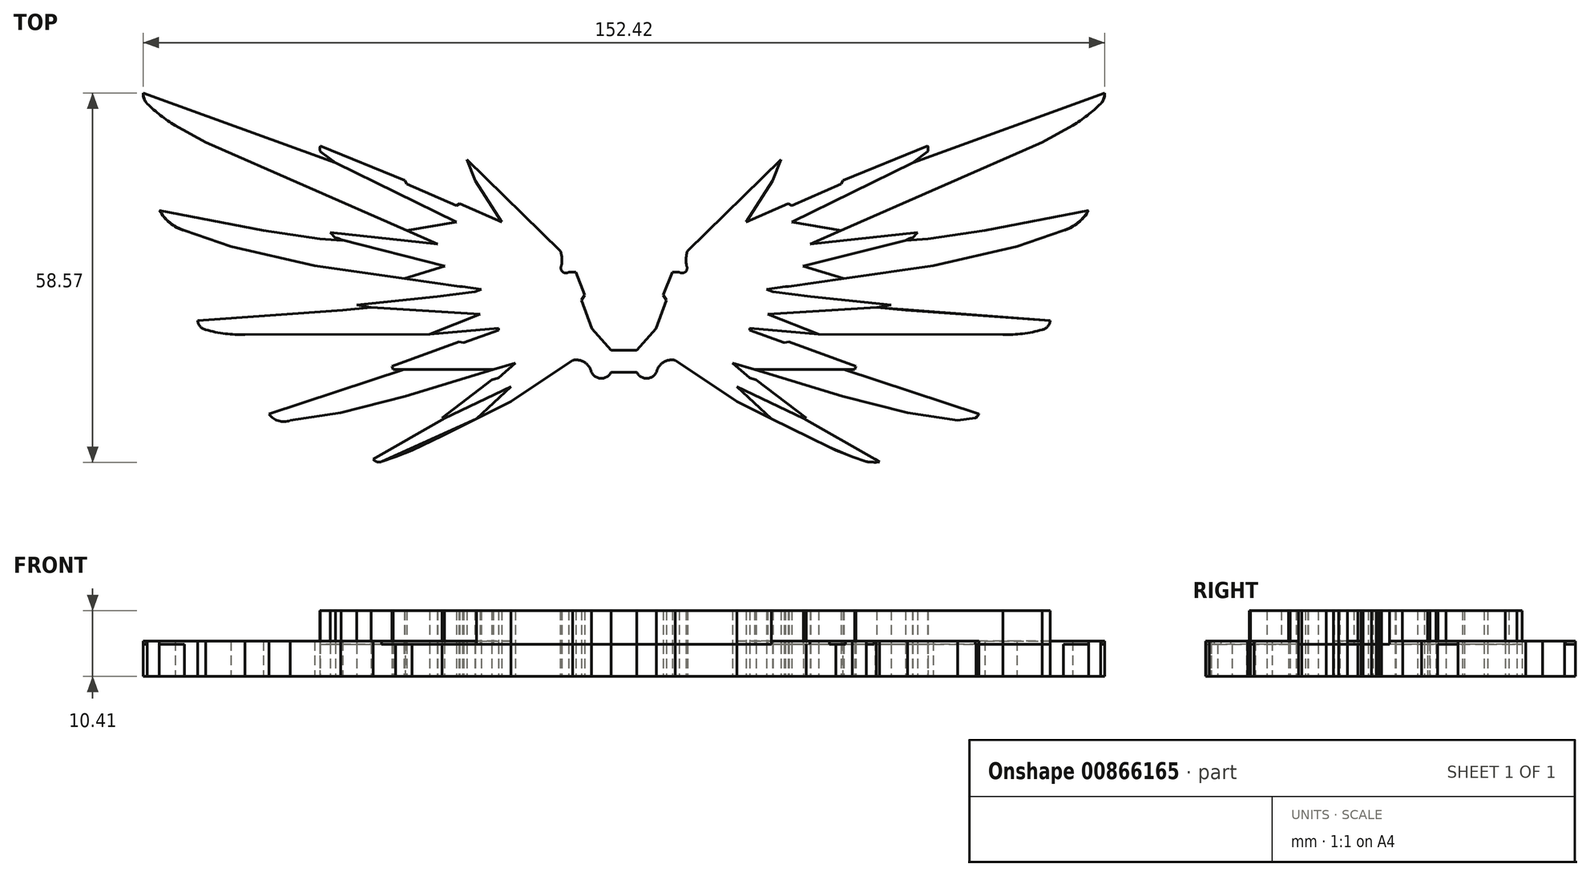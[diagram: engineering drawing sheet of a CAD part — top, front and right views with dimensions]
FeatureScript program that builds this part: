
annotation { "Feature Type Name" : "Feature", "Feature Type Description" : "" }
export const myFeature = defineFeature(function(context is Context, id is Id, definition is map)
    precondition{}
    {
        {
            var Q0;
            Q0=qCreatedBy(makeId("Top.planeOp"),FACE);
            var sketch = newSketch(context, id + "F0", { "sketchPlane" : qUnion([Q0])});
            skLineSegment(sketch, "E0", {"start": v(-45.75, 18.62) * mm, "end": v(-76.2, 29.69) * mm});
            skArc(sketch, "E1", {"start": v(-76.2, 29.69) * mm, "mid": v(-76.09, 28.76) * mm, "end": v(-75.56, 27.98) * mm});
            skArc(sketch, "E2", {"start": v(-75.56, 27.98) * mm, "mid": v(-73.45, 26.13) * mm, "end": v(-71.14, 24.54) * mm});
            skLineSegment(sketch, "E3", {"start": v(-71.14, 24.54) * mm, "end": v(-66.27, 21.85) * mm});
            skLineSegment(sketch, "E4", {"start": v(-66.27, 21.85) * mm, "end": v(-58.56, 18.47) * mm});
            skLineSegment(sketch, "E5", {"start": v(-58.56, 18.47) * mm, "end": v(-35.36, 8.31) * mm});
            skLineSegment(sketch, "E6", {"start": v(-35.36, 8.31) * mm, "end": v(-29.5, 5.75) * mm});
            skLineSegment(sketch, "E7", {"start": v(-29.5, 5.75) * mm, "end": v(-46.28, 7.57) * mm});
            skLineSegment(sketch, "E8", {"start": v(-46.28, 7.57) * mm, "end": v(-46.55, 7.6) * mm});
            skLineSegment(sketch, "E9", {"start": v(-46.55, 7.6) * mm, "end": v(-45.74, 6.68) * mm});
            skArc(sketch, "E10", {"start": v(-44.62, 6.28) * mm, "mid": v(-45.14, 6.59) * mm, "end": v(-45.74, 6.68) * mm});
            skLineSegment(sketch, "E11", {"start": v(-44.62, 6.28) * mm, "end": v(-48.2, 6.59) * mm});
            skLineSegment(sketch, "E12", {"start": v(-48.2, 6.59) * mm, "end": v(-57.18, 7.91) * mm});
            skLineSegment(sketch, "E13", {"start": v(-57.18, 7.91) * mm, "end": v(-73.65, 11.1) * mm});
            skArc(sketch, "E14", {"start": v(-73.65, 11.1) * mm, "mid": v(-71.99, 9.08) * mm, "end": v(-69.68, 7.87) * mm});
            skLineSegment(sketch, "E15", {"start": v(-69.68, 7.87) * mm, "end": v(-62.27, 5.33) * mm});
            skLineSegment(sketch, "E16", {"start": v(-62.27, 5.33) * mm, "end": v(-49, 2.32) * mm});
            skLineSegment(sketch, "E17", {"start": v(-49, 2.32) * mm, "end": v(-26.07, -1) * mm});
            skLineSegment(sketch, "E18", {"start": v(-25.58, -1) * mm, "end": v(-26.07, -1) * mm});
            skLineSegment(sketch, "E19", {"start": v(-25.58, -1) * mm, "end": v(-22.58, -1.44) * mm});
            skLineSegment(sketch, "E20", {"start": v(-22.58, -1.44) * mm, "end": v(-23.6, -1.82) * mm});
            skLineSegment(sketch, "E21", {"start": v(-23.6, -1.82) * mm, "end": v(-29.6, -2.6) * mm});
            skLineSegment(sketch, "E22", {"start": v(-29.6, -2.6) * mm, "end": v(-42.37, -3.94) * mm});
            skLineSegment(sketch, "E23", {"start": v(-42.37, -3.94) * mm, "end": v(-40.05, -4.27) * mm});
            skLineSegment(sketch, "E24", {"start": v(-40.05, -4.27) * mm, "end": v(-44.6, -4.75) * mm});
            skLineSegment(sketch, "E25", {"start": v(-44.6, -4.75) * mm, "end": v(-67.56, -6.41) * mm});
            skArc(sketch, "E26", {"start": v(-67.56, -6.41) * mm, "mid": v(-67.16, -7.34) * mm, "end": v(-66.27, -7.83) * mm});
            skArc(sketch, "E27", {"start": v(-66.27, -7.83) * mm, "mid": v(-63.2, -8.47) * mm, "end": v(-60.07, -8.59) * mm});
            skLineSegment(sketch, "E28", {"start": v(-45.75, 18.62) * mm, "end": v(-48.16, 20.42) * mm});
            skArc(sketch, "E29", {"start": v(-48.16, 21.28) * mm, "mid": v(-48.19, 20.85) * mm, "end": v(-48.16, 20.42) * mm});
            skLineSegment(sketch, "E30", {"start": v(-48.16, 21.28) * mm, "end": v(-34.72, 15.82) * mm});
            skLineSegment(sketch, "E31", {"start": v(-34.72, 15.82) * mm, "end": v(-34.44, 15.24) * mm});
            skLineSegment(sketch, "E32", {"start": v(-34.44, 15.24) * mm, "end": v(-26.57, 11.84) * mm});
            skLineSegment(sketch, "E33", {"start": v(-26.57, 11.84) * mm, "end": v(-26.05, 12.12) * mm});
            skLineSegment(sketch, "E34", {"start": v(-26.05, 12.12) * mm, "end": v(-19.34, 9.23) * mm});
            skLineSegment(sketch, "E35", {"start": v(-19.34, 9.23) * mm, "end": v(-23.55, 15.8) * mm});
            skLineSegment(sketch, "E36", {"start": v(-23.55, 15.8) * mm, "end": v(-24.88, 19.15) * mm});
            skLineSegment(sketch, "E37", {"start": v(-24.88, 19.15) * mm, "end": v(-10.07, 4.67) * mm});
            skArc(sketch, "E38", {"start": v(-9.92, 2.28) * mm, "mid": v(-9.85, 3.48) * mm, "end": v(-10.07, 4.67) * mm});
            skArc(sketch, "E39", {"start": v(-9.92, 2.28) * mm, "mid": v(-9.74, 1.34) * mm, "end": v(-8.79, 1.28) * mm});
            skLineSegment(sketch, "E40", {"start": v(-8.79, 1.28) * mm, "end": v(-7.65, 1.28) * mm});
            skLineSegment(sketch, "E41", {"start": v(-7.65, 1.28) * mm, "end": v(-6.25, -2.35) * mm});
            skLineSegment(sketch, "E42", {"start": v(-6.25, -2.35) * mm, "end": v(-6.74, -3.13) * mm});
            skLineSegment(sketch, "E43", {"start": v(-6.74, -3.13) * mm, "end": v(-5.06, -7.67) * mm});
            skLineSegment(sketch, "E44", {"start": v(-5.06, -7.67) * mm, "end": v(-2.02, -11.07) * mm});
            skLineSegment(sketch, "E45", {"start": v(-2.02, -11.07) * mm, "end": v(-2.02, -12.75) * mm});
            skLineSegment(sketch, "E46", {"start": v(-2.02, -12.75) * mm, "end": v(-2.02, -14.56) * mm});
            skArc(sketch, "E47", {"start": v(-5.16, -14.56) * mm, "mid": v(-3.59, -15.55) * mm, "end": v(-2.02, -14.56) * mm});
            skArc(sketch, "E48", {"start": v(-5.16, -14.56) * mm, "mid": v(-6.25, -13) * mm, "end": v(-8.13, -12.69) * mm});
            skLineSegment(sketch, "E49", {"start": v(-60.07, -8.59) * mm, "end": v(-30.83, -8.52) * mm});
            skLineSegment(sketch, "E50", {"start": v(-30.83, -8.52) * mm, "end": v(-19.9, -7.62) * mm});
            skLineSegment(sketch, "E51", {"start": v(-19.9, -7.62) * mm, "end": v(-19.9, -7.95) * mm});
            skLineSegment(sketch, "E52", {"start": v(-19.9, -7.95) * mm, "end": v(-25.4, -9.9) * mm});
            skLineSegment(sketch, "E53", {"start": v(-25.4, -9.9) * mm, "end": v(-26.18, -9.79) * mm});
            skLineSegment(sketch, "E54", {"start": v(-26.18, -9.79) * mm, "end": v(-36.78, -13.62) * mm});
            skLineSegment(sketch, "E55", {"start": v(-36.78, -13.62) * mm, "end": v(-36.59, -14.16) * mm});
            skLineSegment(sketch, "E56", {"start": v(-36.59, -14.16) * mm, "end": v(-34.87, -14.16) * mm});
            skLineSegment(sketch, "E57", {"start": v(-34.87, -14.16) * mm, "end": v(-56.27, -21.21) * mm});
            skLineSegment(sketch, "E58", {"start": v(-52.88, -22.23) * mm, "end": v(-44.92, -21.03) * mm});
            skLineSegment(sketch, "E59", {"start": v(-44.92, -21.03) * mm, "end": v(-34.68, -18.38) * mm});
            skLineSegment(sketch, "E60", {"start": v(-34.68, -18.38) * mm, "end": v(-17.22, -13.1) * mm});
            skLineSegment(sketch, "E61", {"start": v(-17.22, -13.1) * mm, "end": v(-19.9, -15.47) * mm});
            skLineSegment(sketch, "E62", {"start": v(-19.9, -15.47) * mm, "end": v(-20.95, -15.78) * mm});
            skLineSegment(sketch, "E63", {"start": v(-20.95, -15.78) * mm, "end": v(-28.86, -21.8) * mm});
            skLineSegment(sketch, "E64", {"start": v(-28.86, -21.8) * mm, "end": v(-28.42, -21.87) * mm});
            skLineSegment(sketch, "E65", {"start": v(-28.42, -21.87) * mm, "end": v(-39.78, -28.34) * mm});
            skLineSegment(sketch, "E66", {"start": v(-38.42, -28.77) * mm, "end": v(-36.2, -27.99) * mm});
            skLineSegment(sketch, "E67", {"start": v(-36.2, -27.99) * mm, "end": v(-33.59, -26.98) * mm});
            skLineSegment(sketch, "E68", {"start": v(-33.59, -26.98) * mm, "end": v(-28.86, -24.68) * mm});
            skLineSegment(sketch, "E69", {"start": v(-28.86, -24.68) * mm, "end": v(-17.91, -19.2) * mm});
            skLineSegment(sketch, "E70", {"start": v(-17.91, -19.2) * mm, "end": v(-8.13, -12.69) * mm});
            skLineSegment(sketch, "E71.MirrorCS", {"start": v(46.28, 7.57) * mm, "end": v(46.55, 7.6) * mm});
            skLineSegment(sketch, "E72.MirrorCS", {"start": v(28.86, -21.8) * mm, "end": v(28.42, -21.87) * mm});
            skLineSegment(sketch, "E73.MirrorCS", {"start": v(38.42, -28.77) * mm, "end": v(36.2, -27.99) * mm});
            skLineSegment(sketch, "E74.MirrorCS", {"start": v(34.72, 15.82) * mm, "end": v(34.44, 15.24) * mm});
            skLineSegment(sketch, "E75.MirrorCS", {"start": v(40.03, -28.88) * mm, "end": v(38.42, -28.77) * mm});
            skLineSegment(sketch, "E76.MirrorCS", {"start": v(25.4, -9.9) * mm, "end": v(26.18, -9.79) * mm});
            skArc(sketch, "E77.MirrorCS", {"start": v(44.62, 6.28) * mm, "mid": v(45.14, 6.59) * mm, "end": v(45.74, 6.68) * mm});
            skLineSegment(sketch, "E78.MirrorCS", {"start": v(46.55, 7.6) * mm, "end": v(45.74, 6.68) * mm});
            skLineSegment(sketch, "E79.MirrorCS", {"start": v(40.52, -28.8) * mm, "end": v(40.03, -28.88) * mm});
            skLineSegment(sketch, "E80.MirrorCS", {"start": v(44.62, 6.28) * mm, "end": v(48.2, 6.59) * mm});
            skLineSegment(sketch, "E81.MirrorCS", {"start": v(25.58, -1) * mm, "end": v(26.07, -1) * mm});
            skLineSegment(sketch, "E82.MirrorCS", {"start": v(22.58, -1.44) * mm, "end": v(23.6, -1.82) * mm});
            skLineSegment(sketch, "E83.MirrorCS", {"start": v(39.78, -28.34) * mm, "end": v(40.52, -28.8) * mm});
            skArc(sketch, "E84.MirrorCS", {"start": v(9.92, 2.28) * mm, "mid": v(9.74, 1.34) * mm, "end": v(8.79, 1.28) * mm});
            skLineSegment(sketch, "E85.MirrorCS", {"start": v(25.58, -1) * mm, "end": v(22.58, -1.44) * mm});
            skArc(sketch, "E86.MirrorCS", {"start": v(5.16, -14.56) * mm, "mid": v(3.59, -15.55) * mm, "end": v(2.02, -14.56) * mm});
            skLineSegment(sketch, "E87.MirrorCS", {"start": v(2.02, -12.75) * mm, "end": v(2.02, -14.56) * mm});
            skLineSegment(sketch, "E88.MirrorCS", {"start": v(19.9, -7.62) * mm, "end": v(19.9, -7.95) * mm});
            skLineSegment(sketch, "E89.MirrorCS", {"start": v(8.79, 1.28) * mm, "end": v(7.65, 1.28) * mm});
            skLineSegment(sketch, "E90.MirrorCS", {"start": v(56.27, -21.21) * mm, "end": v(55.84, -21.8) * mm});
            skArc(sketch, "E91.MirrorCS", {"start": v(76.2, 29.69) * mm, "mid": v(76.09, 28.76) * mm, "end": v(75.56, 27.98) * mm});
            skLineSegment(sketch, "E92.MirrorCS", {"start": v(30.83, -8.52) * mm, "end": v(19.9, -7.62) * mm});
            skLineSegment(sketch, "E93.MirrorCS", {"start": v(36.2, -27.99) * mm, "end": v(33.59, -26.98) * mm});
            skLineSegment(sketch, "E94.MirrorCS", {"start": v(23.6, -1.82) * mm, "end": v(29.6, -2.6) * mm});
            skLineSegment(sketch, "E95.MirrorCS", {"start": v(40.05, -4.27) * mm, "end": v(44.6, -4.75) * mm});
            skLineSegment(sketch, "E96.MirrorCS", {"start": v(42.37, -3.94) * mm, "end": v(40.05, -4.27) * mm});
            skLineSegment(sketch, "E97.MirrorCS", {"start": v(5.06, -7.67) * mm, "end": v(2.02, -11.07) * mm});
            skLineSegment(sketch, "E98.MirrorCS", {"start": v(55.84, -21.8) * mm, "end": v(52.88, -22.23) * mm});
            skLineSegment(sketch, "E99.MirrorCS", {"start": v(36.78, -13.62) * mm, "end": v(36.59, -14.16) * mm});
            skLineSegment(sketch, "E100.MirrorCS", {"start": v(19.9, -15.47) * mm, "end": v(20.95, -15.78) * mm});
            skArc(sketch, "E101.MirrorCS", {"start": v(73.65, 11.1) * mm, "mid": v(71.99, 9.08) * mm, "end": v(69.68, 7.87) * mm});
            skLineSegment(sketch, "E102.MirrorCS", {"start": v(35.36, 8.31) * mm, "end": v(29.5, 5.75) * mm});
            skLineSegment(sketch, "E103.MirrorCS", {"start": v(45.75, 18.62) * mm, "end": v(48.16, 20.42) * mm});
            skArc(sketch, "E104.MirrorCS", {"start": v(66.27, -7.83) * mm, "mid": v(63.2, -8.47) * mm, "end": v(60.07, -8.59) * mm});
            skLineSegment(sketch, "E105.MirrorCS", {"start": v(19.34, 9.23) * mm, "end": v(23.55, 15.8) * mm});
            skLineSegment(sketch, "E106.MirrorCS", {"start": v(6.74, -3.13) * mm, "end": v(5.06, -7.67) * mm});
            skLineSegment(sketch, "E107.MirrorCS", {"start": v(33.59, -26.98) * mm, "end": v(28.86, -24.68) * mm});
            skLineSegment(sketch, "E108.MirrorCS", {"start": v(56.27, -21.21) * mm, "end": v(56.27, -21.21) * mm});
            skLineSegment(sketch, "E109.MirrorCS", {"start": v(71.14, 24.54) * mm, "end": v(66.27, 21.85) * mm});
            skLineSegment(sketch, "E110.MirrorCS", {"start": v(6.25, -2.35) * mm, "end": v(6.74, -3.13) * mm});
            skLineSegment(sketch, "E111.MirrorCS", {"start": v(19.9, -7.95) * mm, "end": v(25.4, -9.9) * mm});
            skArc(sketch, "E112.MirrorCS", {"start": v(75.56, 27.98) * mm, "mid": v(73.45, 26.13) * mm, "end": v(71.14, 24.54) * mm});
            skArc(sketch, "E113.MirrorCS", {"start": v(48.16, 21.28) * mm, "mid": v(48.19, 20.85) * mm, "end": v(48.16, 20.42) * mm});
            skArc(sketch, "E114.MirrorCS", {"start": v(5.16, -14.56) * mm, "mid": v(6.25, -13) * mm, "end": v(8.13, -12.69) * mm});
            skLineSegment(sketch, "E115.MirrorCS", {"start": v(36.59, -14.16) * mm, "end": v(34.87, -14.16) * mm});
            skArc(sketch, "E116.MirrorCS", {"start": v(67.56, -6.41) * mm, "mid": v(67.16, -7.34) * mm, "end": v(66.27, -7.83) * mm});
            skLineSegment(sketch, "E117.MirrorCS", {"start": v(17.22, -13.1) * mm, "end": v(19.9, -15.47) * mm});
            skLineSegment(sketch, "E118.MirrorCS", {"start": v(26.57, 11.84) * mm, "end": v(26.05, 12.12) * mm});
            skLineSegment(sketch, "E119.MirrorCS", {"start": v(23.55, 15.8) * mm, "end": v(24.88, 19.15) * mm});
            skLineSegment(sketch, "E120.MirrorCS", {"start": v(7.65, 1.28) * mm, "end": v(6.25, -2.35) * mm});
            skArc(sketch, "E121.MirrorCS", {"start": v(9.92, 2.28) * mm, "mid": v(9.85, 3.48) * mm, "end": v(10.07, 4.67) * mm});
            skLineSegment(sketch, "E122.MirrorCS", {"start": v(2.02, -11.07) * mm, "end": v(2.02, -12.75) * mm});
            skLineSegment(sketch, "E123.MirrorCS", {"start": v(17.91, -19.2) * mm, "end": v(8.13, -12.69) * mm});
            skLineSegment(sketch, "E124.MirrorCS", {"start": v(20.95, -15.78) * mm, "end": v(28.86, -21.8) * mm});
            skLineSegment(sketch, "E125.MirrorCS", {"start": v(26.05, 12.12) * mm, "end": v(19.34, 9.23) * mm});
            skLineSegment(sketch, "E126.MirrorCS", {"start": v(66.27, 21.85) * mm, "end": v(58.56, 18.47) * mm});
            skLineSegment(sketch, "E127.MirrorCS", {"start": v(34.68, -18.38) * mm, "end": v(17.22, -13.1) * mm});
            skLineSegment(sketch, "E128.MirrorCS", {"start": v(45.75, 18.62) * mm, "end": v(76.2, 29.69) * mm});
            skLineSegment(sketch, "E129.MirrorCS", {"start": v(60.07, -8.59) * mm, "end": v(30.83, -8.52) * mm});
            skLineSegment(sketch, "E130.MirrorCS", {"start": v(48.2, 6.59) * mm, "end": v(57.18, 7.91) * mm});
            skLineSegment(sketch, "E131.MirrorCS", {"start": v(62.27, 5.33) * mm, "end": v(49, 2.32) * mm});
            skLineSegment(sketch, "E132.MirrorCS", {"start": v(29.5, 5.75) * mm, "end": v(46.28, 7.57) * mm});
            skLineSegment(sketch, "E133.MirrorCS", {"start": v(24.88, 19.15) * mm, "end": v(10.07, 4.67) * mm});
            skLineSegment(sketch, "E134.MirrorCS", {"start": v(48.16, 21.28) * mm, "end": v(34.72, 15.82) * mm});
            skLineSegment(sketch, "E135.MirrorCS", {"start": v(52.88, -22.23) * mm, "end": v(44.92, -21.03) * mm});
            skLineSegment(sketch, "E136.MirrorCS", {"start": v(34.87, -14.16) * mm, "end": v(56.27, -21.21) * mm});
            skLineSegment(sketch, "E137.MirrorCS", {"start": v(34.44, 15.24) * mm, "end": v(26.57, 11.84) * mm});
            skLineSegment(sketch, "E138.MirrorCS", {"start": v(69.68, 7.87) * mm, "end": v(62.27, 5.33) * mm});
            skLineSegment(sketch, "E139.MirrorCS", {"start": v(44.6, -4.75) * mm, "end": v(67.56, -6.41) * mm});
            skLineSegment(sketch, "E140.MirrorCS", {"start": v(58.56, 18.47) * mm, "end": v(35.36, 8.31) * mm});
            skLineSegment(sketch, "E141.MirrorCS", {"start": v(28.42, -21.87) * mm, "end": v(39.78, -28.34) * mm});
            skLineSegment(sketch, "E142.MirrorCS", {"start": v(49, 2.32) * mm, "end": v(26.07, -1) * mm});
            skLineSegment(sketch, "E143.MirrorCS", {"start": v(29.6, -2.6) * mm, "end": v(42.37, -3.94) * mm});
            skLineSegment(sketch, "E144.MirrorCS", {"start": v(44.92, -21.03) * mm, "end": v(34.68, -18.38) * mm});
            skLineSegment(sketch, "E145.MirrorCS", {"start": v(26.18, -9.79) * mm, "end": v(36.78, -13.62) * mm});
            skLineSegment(sketch, "E146.MirrorCS", {"start": v(28.86, -24.68) * mm, "end": v(17.91, -19.2) * mm});
            skLineSegment(sketch, "E147.MirrorCS", {"start": v(57.18, 7.91) * mm, "end": v(73.65, 11.1) * mm});
            skArc(sketch, "E148", {"start": v(-39.78, -28.34) * mm, "mid": v(-39.17, -28.79) * mm, "end": v(-38.42, -28.77) * mm});
            skArc(sketch, "E149", {"start": v(-56.27, -21.21) * mm, "mid": v(-54.74, -22.29) * mm, "end": v(-52.88, -22.23) * mm});
            skPoint(sketch, "E150.end.orphan", {"position": v(-55.84, -21.8) * mm});
            skLineSegment(sketch, "E151", {"start": v(2.02, -11.07) * mm, "end": v(-2.02, -11.07) * mm});
            skLineSegment(sketch, "E152", {"start": v(-2.02, -14.56) * mm, "end": v(2.02, -14.56) * mm});
            skSolve(sketch);
        }
        {
            var Q0;
            Q0=makeQuery(id+"F0.imprint","IMPRINT",FACE,{"disambiguationData":[TD([[makeQuery(id+"F0.imprint","IMPRINT",EDGE,{"derivedFrom":sQuery(id+"F0.wireOp",EDGE,"E0")}),1.0]])]});
            var Q1;
            Q1=makeQuery(id+"F0.imprint","IMPRINT",FACE,{"disambiguationData":[TD([[makeQuery(id+"F0.imprint","IMPRINT",EDGE,{"derivedFrom":sQuery(id+"F0.wireOp",EDGE,"E72.MirrorCS")}),-1.0]])]});
            var Q2;
            Q2=makeQuery(id+"F0.imprint","IMPRINT",FACE,{"disambiguationData":[TD([[makeQuery(id+"F0.imprint","IMPRINT",EDGE,{"derivedFrom":sQuery(id+"F0.wireOp",EDGE,"E45")}),1.0]])]});
            extrude(context, id + "F1", {"entities" : qUnion([Q0, Q1, Q2]), "depth" : 5.08 * mm, "offsetDistance" : 25.4 * mm});
        }
        {
            var Q0;
            Q0=makeQuery(id+"F1.opExtrude","CAP_FACE",FACE,{"disambiguationData":[OSD([sQuery(id+"F0.wireOp",EDGE,"E0"),sQuery(id+"F0.wireOp",EDGE,"E1"),sQuery(id+"F0.wireOp",EDGE,"E2"),sQuery(id+"F0.wireOp",EDGE,"E3"),sQuery(id+"F0.wireOp",EDGE,"E4"),sQuery(id+"F0.wireOp",EDGE,"E5"),sQuery(id+"F0.wireOp",EDGE,"E6"),sQuery(id+"F0.wireOp",EDGE,"E7"),sQuery(id+"F0.wireOp",EDGE,"E8"),sQuery(id+"F0.wireOp",EDGE,"E9"),sQuery(id+"F0.wireOp",EDGE,"E10"),sQuery(id+"F0.wireOp",EDGE,"E11"),sQuery(id+"F0.wireOp",EDGE,"E12"),sQuery(id+"F0.wireOp",EDGE,"E13"),sQuery(id+"F0.wireOp",EDGE,"E14"),sQuery(id+"F0.wireOp",EDGE,"E15"),sQuery(id+"F0.wireOp",EDGE,"E16"),sQuery(id+"F0.wireOp",EDGE,"E17"),sQuery(id+"F0.wireOp",EDGE,"E18"),sQuery(id+"F0.wireOp",EDGE,"E19"),sQuery(id+"F0.wireOp",EDGE,"E20"),sQuery(id+"F0.wireOp",EDGE,"E21"),sQuery(id+"F0.wireOp",EDGE,"E22"),sQuery(id+"F0.wireOp",EDGE,"E23"),sQuery(id+"F0.wireOp",EDGE,"E24"),sQuery(id+"F0.wireOp",EDGE,"E25"),sQuery(id+"F0.wireOp",EDGE,"E26"),sQuery(id+"F0.wireOp",EDGE,"E27"),sQuery(id+"F0.wireOp",EDGE,"E28"),sQuery(id+"F0.wireOp",EDGE,"E29"),sQuery(id+"F0.wireOp",EDGE,"E30"),sQuery(id+"F0.wireOp",EDGE,"E31"),sQuery(id+"F0.wireOp",EDGE,"E32"),sQuery(id+"F0.wireOp",EDGE,"E33"),sQuery(id+"F0.wireOp",EDGE,"E34"),sQuery(id+"F0.wireOp",EDGE,"E35"),sQuery(id+"F0.wireOp",EDGE,"E36"),sQuery(id+"F0.wireOp",EDGE,"E37"),sQuery(id+"F0.wireOp",EDGE,"E38"),sQuery(id+"F0.wireOp",EDGE,"E39"),sQuery(id+"F0.wireOp",EDGE,"E40"),sQuery(id+"F0.wireOp",EDGE,"E41"),sQuery(id+"F0.wireOp",EDGE,"E42"),sQuery(id+"F0.wireOp",EDGE,"E43"),sQuery(id+"F0.wireOp",EDGE,"E44"),sQuery(id+"F0.wireOp",EDGE,"E45"),sQuery(id+"F0.wireOp",EDGE,"E46"),sQuery(id+"F0.wireOp",EDGE,"E47"),sQuery(id+"F0.wireOp",EDGE,"E48"),sQuery(id+"F0.wireOp",EDGE,"E49"),sQuery(id+"F0.wireOp",EDGE,"E50"),sQuery(id+"F0.wireOp",EDGE,"E51"),sQuery(id+"F0.wireOp",EDGE,"E52"),sQuery(id+"F0.wireOp",EDGE,"E53"),sQuery(id+"F0.wireOp",EDGE,"E54"),sQuery(id+"F0.wireOp",EDGE,"E55"),sQuery(id+"F0.wireOp",EDGE,"E56"),sQuery(id+"F0.wireOp",EDGE,"E57"),sQuery(id+"F0.wireOp",EDGE,"E58"),sQuery(id+"F0.wireOp",EDGE,"E59"),sQuery(id+"F0.wireOp",EDGE,"E60"),sQuery(id+"F0.wireOp",EDGE,"E61"),sQuery(id+"F0.wireOp",EDGE,"E62"),sQuery(id+"F0.wireOp",EDGE,"E63"),sQuery(id+"F0.wireOp",EDGE,"E64"),sQuery(id+"F0.wireOp",EDGE,"E65"),sQuery(id+"F0.wireOp",EDGE,"E66"),sQuery(id+"F0.wireOp",EDGE,"E67"),sQuery(id+"F0.wireOp",EDGE,"E68"),sQuery(id+"F0.wireOp",EDGE,"E69"),sQuery(id+"F0.wireOp",EDGE,"E70"),sQuery(id+"F0.wireOp",EDGE,"E148"),sQuery(id+"F0.wireOp",EDGE,"E149")])],"isStart":false});
            var sketch = newSketch(context, id + "F2", { "sketchPlane" : qUnion([Q0])});
            skLineSegment(sketch, "E153", {"start": v(-76.2, 29.69) * mm, "end": v(-45.75, 18.62) * mm});
            skLineSegment(sketch, "E154", {"start": v(-45.75, 18.62) * mm, "end": v(-26.57, 9.23) * mm});
            skLineSegment(sketch, "E155", {"start": v(-26.57, 9.23) * mm, "end": v(-34.44, 7.9) * mm});
            skLineSegment(sketch, "E156", {"start": v(-34.44, 7.9) * mm, "end": v(-66.27, 21.85) * mm});
            skArc(sketch, "E157", {"start": v(-73.65, 11.1) * mm, "mid": v(-71.95, 9.13) * mm, "end": v(-69.68, 7.87) * mm});
            skArc(sketch, "E158", {"start": v(-56.27, -21.21) * mm, "mid": v(-54.75, -22.3) * mm, "end": v(-52.88, -22.23) * mm});
            skArc(sketch, "E159", {"start": v(-39.78, -28.34) * mm, "mid": v(-39.17, -28.79) * mm, "end": v(-38.42, -28.77) * mm});
            skArc(sketch, "E160", {"start": v(-76.2, 29.69) * mm, "mid": v(-75.76, 28.2) * mm, "end": v(-74.65, 27.13) * mm});
            skArc(sketch, "E161", {"start": v(-74.65, 27.13) * mm, "mid": v(-72.98, 25.72) * mm, "end": v(-71.14, 24.54) * mm});
            skLineSegment(sketch, "E162", {"start": v(-71.14, 24.54) * mm, "end": v(-66.27, 21.85) * mm});
            skLineSegment(sketch, "E163", {"start": v(-73.65, 11.1) * mm, "end": v(-45.74, 6.68) * mm});
            skLineSegment(sketch, "E164", {"start": v(-45.74, 6.68) * mm, "end": v(-28.4, 2.26) * mm});
            skLineSegment(sketch, "E165", {"start": v(-28.4, 2.26) * mm, "end": v(-34.83, 0.27) * mm});
            skLineSegment(sketch, "E166", {"start": v(-34.83, 0.27) * mm, "end": v(-49, 2.32) * mm});
            skLineSegment(sketch, "E167", {"start": v(-49, 2.32) * mm, "end": v(-62.27, 5.33) * mm});
            skLineSegment(sketch, "E168", {"start": v(-62.27, 5.33) * mm, "end": v(-69.68, 7.87) * mm});
            skLineSegment(sketch, "E169", {"start": v(-30.83, -8.52) * mm, "end": v(-60.07, -8.59) * mm});
            skLineSegment(sketch, "E170", {"start": v(-30.83, -8.52) * mm, "end": v(-22.8, -5.37) * mm});
            skLineSegment(sketch, "E171", {"start": v(-22.8, -5.37) * mm, "end": v(-40.05, -4.27) * mm});
            skLineSegment(sketch, "E172", {"start": v(-40.05, -4.27) * mm, "end": v(-67.56, -6.41) * mm});
            skLineSegment(sketch, "E173", {"start": v(-56.27, -21.21) * mm, "end": v(-34.87, -14.16) * mm});
            skLineSegment(sketch, "E174", {"start": v(-34.87, -14.16) * mm, "end": v(-20.71, -14.16) * mm});
            skLineSegment(sketch, "E175", {"start": v(-20.71, -14.16) * mm, "end": v(-34.68, -18.38) * mm});
            skLineSegment(sketch, "E176", {"start": v(-34.68, -18.38) * mm, "end": v(-44.92, -21.03) * mm});
            skLineSegment(sketch, "E177", {"start": v(-44.92, -21.03) * mm, "end": v(-52.88, -22.23) * mm});
            skLineSegment(sketch, "E178", {"start": v(-28.42, -21.87) * mm, "end": v(-17.91, -16.89) * mm});
            skLineSegment(sketch, "E179", {"start": v(-17.91, -16.89) * mm, "end": v(-23.39, -21.94) * mm});
            skLineSegment(sketch, "E180.MirrorCS", {"start": v(45.75, 18.62) * mm, "end": v(26.57, 9.23) * mm});
            skLineSegment(sketch, "E181.MirrorCS", {"start": v(26.57, 9.23) * mm, "end": v(34.44, 7.9) * mm});
            skLineSegment(sketch, "E182.MirrorCS", {"start": v(34.44, 7.9) * mm, "end": v(66.27, 21.85) * mm});
            skLineSegment(sketch, "E183.MirrorCS", {"start": v(71.14, 24.54) * mm, "end": v(66.27, 21.85) * mm});
            skArc(sketch, "E184.MirrorCS", {"start": v(74.65, 27.13) * mm, "mid": v(72.98, 25.72) * mm, "end": v(71.14, 24.54) * mm});
            skArc(sketch, "E185.MirrorCS", {"start": v(76.2, 29.69) * mm, "mid": v(75.76, 28.2) * mm, "end": v(74.65, 27.13) * mm});
            skLineSegment(sketch, "E186.MirrorCS", {"start": v(76.2, 29.69) * mm, "end": v(45.75, 18.62) * mm});
            skLineSegment(sketch, "E187.MirrorCS", {"start": v(28.4, 2.26) * mm, "end": v(34.83, 0.27) * mm});
            skLineSegment(sketch, "E188.MirrorCS", {"start": v(34.83, 0.27) * mm, "end": v(49, 2.32) * mm});
            skLineSegment(sketch, "E189.MirrorCS", {"start": v(49, 2.32) * mm, "end": v(62.27, 5.33) * mm});
            skLineSegment(sketch, "E190.MirrorCS", {"start": v(62.27, 5.33) * mm, "end": v(69.68, 7.87) * mm});
            skArc(sketch, "E191.MirrorCS", {"start": v(73.65, 11.1) * mm, "mid": v(71.95, 9.13) * mm, "end": v(69.68, 7.87) * mm});
            skLineSegment(sketch, "E192.MirrorCS", {"start": v(40.05, -4.27) * mm, "end": v(67.56, -6.41) * mm});
            skLineSegment(sketch, "E193.MirrorCS", {"start": v(22.8, -5.37) * mm, "end": v(40.05, -4.27) * mm});
            skLineSegment(sketch, "E194.MirrorCS", {"start": v(30.83, -8.52) * mm, "end": v(22.8, -5.37) * mm});
            skLineSegment(sketch, "E195.MirrorCS", {"start": v(34.87, -14.16) * mm, "end": v(20.71, -14.16) * mm});
            skLineSegment(sketch, "E196.MirrorCS", {"start": v(56.27, -21.21) * mm, "end": v(34.87, -14.16) * mm});
            skLineSegment(sketch, "E197.MirrorCS", {"start": v(20.71, -14.16) * mm, "end": v(34.68, -18.38) * mm});
            skLineSegment(sketch, "E198.MirrorCS", {"start": v(34.68, -18.38) * mm, "end": v(44.92, -21.03) * mm});
            skLineSegment(sketch, "E199.MirrorCS", {"start": v(44.92, -21.03) * mm, "end": v(52.88, -22.23) * mm});
            skArc(sketch, "E200.MirrorCS", {"start": v(56.27, -21.21) * mm, "mid": v(54.75, -22.3) * mm, "end": v(52.88, -22.23) * mm});
            skLineSegment(sketch, "E201.MirrorCS", {"start": v(17.91, -16.89) * mm, "end": v(23.39, -21.94) * mm});
            skLineSegment(sketch, "E202.MirrorCS", {"start": v(28.42, -21.87) * mm, "end": v(17.91, -16.89) * mm});
            skLineSegment(sketch, "E203", {"start": v(-23.39, -21.94) * mm, "end": v(-38.42, -28.77) * mm});
            skLineSegment(sketch, "E204", {"start": v(-39.78, -28.34) * mm, "end": v(-29.79, -22.64) * mm});
            skLineSegment(sketch, "E205", {"start": v(-29.79, -22.64) * mm, "end": v(-28.42, -21.87) * mm});
            skLineSegment(sketch, "E206", {"start": v(28.42, -21.87) * mm, "end": v(39.78, -28.34) * mm});
            skLineSegment(sketch, "E207", {"start": v(23.39, -21.94) * mm, "end": v(31.97, -26.23) * mm});
            skLineSegment(sketch, "E208", {"start": v(31.97, -26.23) * mm, "end": v(36.24, -28.04) * mm});
            skLineSegment(sketch, "E209", {"start": v(36.24, -28.04) * mm, "end": v(38.42, -28.77) * mm});
            skArc(sketch, "E210", {"start": v(40.02, -28.9) * mm, "mid": v(39.22, -28.82) * mm, "end": v(38.42, -28.77) * mm});
            skLineSegment(sketch, "E211", {"start": v(39.78, -28.34) * mm, "end": v(40.56, -28.81) * mm});
            skLineSegment(sketch, "E212", {"start": v(40.02, -28.9) * mm, "end": v(40.56, -28.81) * mm});
            skLineSegment(sketch, "E213", {"start": v(30.83, -8.52) * mm, "end": v(63, -8.52) * mm});
            skLineSegment(sketch, "E214", {"start": v(63, -8.52) * mm, "end": v(65.32, -8) * mm});
            skArc(sketch, "E215", {"start": v(65.32, -8) * mm, "mid": v(66.6, -7.43) * mm, "end": v(67.56, -6.41) * mm});
            skLineSegment(sketch, "E216", {"start": v(28.4, 2.26) * mm, "end": v(44.65, 6.28) * mm});
            skLineSegment(sketch, "E217", {"start": v(44.65, 6.28) * mm, "end": v(73.65, 11.1) * mm});
            skSolve(sketch);
        }
        {
            var Q0;
            Q0=makeQuery(id+"F2.imprint","IMPRINT",FACE,{"disambiguationData":[TD([[makeQuery(id+"F2.imprint","IMPRINT",EDGE,{"derivedFrom":sQuery(id+"F2.wireOp",EDGE,"E181.MirrorCS")}),1.0]])]});
            var Q1;
            Q1=makeQuery(id+"F2.imprint","IMPRINT",FACE,{"disambiguationData":[TD([[makeQuery(id+"F2.imprint","IMPRINT",EDGE,{"derivedFrom":sQuery(id+"F2.wireOp",EDGE,"E187.MirrorCS")}),1.0]])]});
            var Q2;
            Q2=makeQuery(id+"F2.imprint","IMPRINT",FACE,{"disambiguationData":[TD([[makeQuery(id+"F2.imprint","IMPRINT",EDGE,{"derivedFrom":sQuery(id+"F2.wireOp",EDGE,"E192.MirrorCS")}),-1.0]])]});
            var Q3;
            Q3=makeQuery(id+"F2.imprint","IMPRINT",FACE,{"disambiguationData":[TD([[makeQuery(id+"F2.imprint","IMPRINT",EDGE,{"derivedFrom":sQuery(id+"F2.wireOp",EDGE,"E195.MirrorCS")}),1.0]])]});
            var Q4;
            Q4=makeQuery(id+"F2.imprint","IMPRINT",FACE,{"disambiguationData":[TD([[makeQuery(id+"F2.imprint","IMPRINT",EDGE,{"derivedFrom":sQuery(id+"F2.wireOp",EDGE,"E202.MirrorCS")}),1.0]])]});
            var Q5;
            {var subQ7=sQuery(id+"F2.wireOp",EDGE,"E153");Q5=makeQuery(id+"F2.imprint","IMPRINT",FACE,{"disambiguationData":[TD([[makeQuery(id+"F2.imprint","IMPRINT",EDGE,{"derivedFrom":subQ7}),1.0]])]});}
            var Q6;
            Q6=makeQuery(id+"F2.imprint","IMPRINT",FACE,{"disambiguationData":[TD([[makeQuery(id+"F2.imprint","IMPRINT",EDGE,{"derivedFrom":sQuery(id+"F2.wireOp",EDGE,"E157")}),1.0]])]});
            var Q7;
            Q7=makeQuery(id+"F2.imprint","IMPRINT",FACE,{"disambiguationData":[TD([[makeQuery(id+"F2.imprint","IMPRINT",EDGE,{"derivedFrom":sQuery(id+"F2.wireOp",EDGE,"E169")}),1.0]])]});
            var Q8;
            Q8=makeQuery(id+"F2.imprint","IMPRINT",FACE,{"disambiguationData":[TD([[makeQuery(id+"F2.imprint","IMPRINT",EDGE,{"derivedFrom":sQuery(id+"F2.wireOp",EDGE,"E173")}),1.0]])]});
            var Q9;
            Q9=makeQuery(id+"F2.imprint","IMPRINT",FACE,{"disambiguationData":[TD([[makeQuery(id+"F2.imprint","IMPRINT",EDGE,{"derivedFrom":sQuery(id+"F2.wireOp",EDGE,"E159")}),1.0]])]});
            extrude(context, id + "F3", {"entities" : qUnion([Q0, Q1, Q2, Q3, Q4, Q5, Q6, Q7, Q8, Q9]), "operationType" : NewBodyOperationType.ADD, "depth" : 0.5 * mm, "offsetDistance" : 25.4 * mm});
        }
        {
            var Q0;
            Q0=makeQuery(id+"F2.imprint","IMPRINT",FACE,{"disambiguationData":[TD([[makeQuery(id+"F2.imprint","IMPRINT",EDGE,{"derivedFrom":sQuery(id+"F2.wireOp",EDGE,"E154")}),1.0]])]});
            var Q1;
            {var subQ0=sQuery(id+"F0.wireOp",EDGE,"E126.MirrorCS");var subQ1=sQuery(id+"F0.wireOp",EDGE,"E140.MirrorCS");var subQ2=sQuery(id+"F0.wireOp",EDGE,"E102.MirrorCS");var subQ3=sQuery(id+"F0.wireOp",EDGE,"E85.MirrorCS");var subQ4=sQuery(id+"F0.wireOp",EDGE,"E119.MirrorCS");var subQ5=sQuery(id+"F0.wireOp",EDGE,"E113.MirrorCS");var subQ6=sQuery(id+"F2.wireOp",EDGE,"E217");var subQ7=sQuery(id+"F0.wireOp",EDGE,"E96.MirrorCS");var subQ8=sQuery(id+"FXjTdA3ObaktCCJ_2.wireOp",EDGE,"JgAZlRST-ak61-B76m-Xn41-PElffQ3qAIJq");var subQ9=sQuery(id+"F2.wireOp",EDGE,"E188.MirrorCS");var subQ10=sQuery(id+"F0.wireOp",EDGE,"E74.MirrorCS");var subQ11=sQuery(id+"FXjTdA3ObaktCCJ_2.wireOp",EDGE,"nxQv954c-nkYm-tbXQ-5Vxz-9EG5dE2x7ZaM");var subQ12=sQuery(id+"F2.wireOp",EDGE,"E216");var subQ13=sQuery(id+"F0.wireOp",EDGE,"E103.MirrorCS");var subQ14=sQuery(id+"FXjTdA3ObaktCCJ_2.wireOp",EDGE,"wds6aXCB-6CSc-TEUh-LF8p-yCgZZW4inpvq");var subQ15=sQuery(id+"FXjTdA3ObaktCCJ_2.wireOp",EDGE,"49gGAReN-EZIu-VxF5-XXtd-cj6RU8iyHlP5");var subQ16=makeQuery(id+"FvTl86mpc58GgTQ_2.opExtrude","CAP_FACE",FACE,{"disambiguationData":[OSD([subQ15,subQ14,subQ11,subQ8])],"isStart":false});var subQ17=sQuery(id+"F0.wireOp",EDGE,"E80.MirrorCS");var subQ18=sQuery(id+"F0.wireOp",EDGE,"E78.MirrorCS");var subQ19=sQuery(id+"F0.wireOp",EDGE,"E77.MirrorCS");var subQ20=sQuery(id+"F0.wireOp",EDGE,"E76.MirrorCS");var subQ21=sQuery(id+"F0.wireOp",EDGE,"E132.MirrorCS");var subQ22=sQuery(id+"F0.wireOp",EDGE,"E71.MirrorCS");var subQ23=sQuery(id+"F0.wireOp",EDGE,"E146.MirrorCS");var subQ24=sQuery(id+"F0.wireOp",EDGE,"E145.MirrorCS");var subQ25=sQuery(id+"F0.wireOp",EDGE,"E141.MirrorCS");var subQ26=sQuery(id+"F0.wireOp",EDGE,"E136.MirrorCS");var subQ27=sQuery(id+"F0.wireOp",EDGE,"E133.MirrorCS");var subQ28=sQuery(id+"F0.wireOp",EDGE,"E127.MirrorCS");var subQ29=sQuery(id+"F0.wireOp",EDGE,"E125.MirrorCS");var subQ30=sQuery(id+"F0.wireOp",EDGE,"E99.MirrorCS");var subQ31=sQuery(id+"F0.wireOp",EDGE,"E95.MirrorCS");var subQ32=sQuery(id+"F0.wireOp",EDGE,"E97.MirrorCS");var subQ33=sQuery(id+"F2.wireOp",EDGE,"E187.MirrorCS");var subQ34=sQuery(id+"F0.wireOp",EDGE,"E88.MirrorCS");var subQ35=sQuery(id+"F0.wireOp",EDGE,"E122.MirrorCS");var subQ36=sQuery(id+"F0.wireOp",EDGE,"E87.MirrorCS");var subQ37=sQuery(id+"F0.wireOp",EDGE,"E89.MirrorCS");var subQ38=sQuery(id+"F0.wireOp",EDGE,"E82.MirrorCS");var subQ39=sQuery(id+"F2.wireOp",EDGE,"E213");var subQ40=sQuery(id+"F0.wireOp",EDGE,"E72.MirrorCS");var subQ41=sQuery(id+"F0.wireOp",EDGE,"E111.MirrorCS");var subQ42=sQuery(id+"F0.wireOp",EDGE,"E94.MirrorCS");var subQ43=sQuery(id+"F0.wireOp",EDGE,"E92.MirrorCS");var subQ44=sQuery(id+"F0.wireOp",EDGE,"E81.MirrorCS");var subQ45=sQuery(id+"F0.wireOp",EDGE,"E129.MirrorCS");var subQ46=sQuery(id+"F0.wireOp",EDGE,"E128.MirrorCS");var subQ47=sQuery(id+"F0.wireOp",EDGE,"E142.MirrorCS");var subQ48=sQuery(id+"F0.wireOp",EDGE,"E143.MirrorCS");var subQ49=sQuery(id+"F0.wireOp",EDGE,"E134.MirrorCS");var subQ50=sQuery(id+"F0.wireOp",EDGE,"E137.MirrorCS");var subQ51=sQuery(id+"F0.wireOp",EDGE,"E118.MirrorCS");var subQ52=sQuery(id+"F0.wireOp",EDGE,"E124.MirrorCS");var subQ53=sQuery(id+"F0.wireOp",EDGE,"E123.MirrorCS");var subQ54=sQuery(id+"F0.wireOp",EDGE,"E121.MirrorCS");var subQ55=sQuery(id+"F0.wireOp",EDGE,"E120.MirrorCS");var subQ56=sQuery(id+"F0.wireOp",EDGE,"E117.MirrorCS");var subQ57=sQuery(id+"F0.wireOp",EDGE,"E115.MirrorCS");var subQ58=sQuery(id+"F0.wireOp",EDGE,"E114.MirrorCS");var subQ59=sQuery(id+"F0.wireOp",EDGE,"E110.MirrorCS");var subQ60=sQuery(id+"F0.wireOp",EDGE,"E106.MirrorCS");var subQ61=sQuery(id+"F0.wireOp",EDGE,"E105.MirrorCS");var subQ62=sQuery(id+"F0.wireOp",EDGE,"E100.MirrorCS");var subQ63=sQuery(id+"F0.wireOp",EDGE,"E86.MirrorCS");var subQ64=sQuery(id+"F0.wireOp",EDGE,"E84.MirrorCS");var subQ65=makeQuery(id+"F1.opExtrude","CAP_FACE",FACE,{"disambiguationData":[OSD([subQ40,sQuery(id+"F0.wireOp",EDGE,"E73.MirrorCS"),sQuery(id+"F0.wireOp",EDGE,"E75.MirrorCS"),sQuery(id+"F0.wireOp",EDGE,"E79.MirrorCS"),sQuery(id+"F0.wireOp",EDGE,"E83.MirrorCS"),subQ64,subQ63,subQ36,subQ34,subQ37,sQuery(id+"F0.wireOp",EDGE,"E90.MirrorCS"),subQ43,sQuery(id+"F0.wireOp",EDGE,"E93.MirrorCS"),subQ32,sQuery(id+"F0.wireOp",EDGE,"E98.MirrorCS"),subQ30,subQ62,subQ61,subQ60,sQuery(id+"F0.wireOp",EDGE,"E107.MirrorCS"),subQ59,subQ41,subQ58,subQ57,subQ56,subQ55,subQ54,subQ35,subQ53,subQ52,subQ29,subQ28,subQ27,sQuery(id+"F0.wireOp",EDGE,"E135.MirrorCS"),subQ26,subQ25,sQuery(id+"F0.wireOp",EDGE,"E144.MirrorCS"),subQ24,subQ23,subQ22,subQ20,subQ19,subQ18,subQ17,sQuery(id+"F0.wireOp",EDGE,"E109.MirrorCS"),sQuery(id+"F0.wireOp",EDGE,"E101.MirrorCS"),subQ38,subQ13,subQ44,subQ10,subQ7,subQ5,subQ4,sQuery(id+"F0.wireOp",EDGE,"E91.MirrorCS"),subQ51,sQuery(id+"F0.wireOp",EDGE,"E104.MirrorCS"),sQuery(id+"F0.wireOp",EDGE,"E116.MirrorCS"),sQuery(id+"F0.wireOp",EDGE,"E112.MirrorCS"),subQ3,subQ42,subQ2,subQ31,subQ21,subQ50,sQuery(id+"F0.wireOp",EDGE,"E131.MirrorCS"),sQuery(id+"F0.wireOp",EDGE,"E130.MirrorCS"),sQuery(id+"F0.wireOp",EDGE,"E139.MirrorCS"),sQuery(id+"F0.wireOp",EDGE,"E147.MirrorCS"),subQ49,subQ1,subQ0,subQ48,sQuery(id+"F0.wireOp",EDGE,"E138.MirrorCS"),subQ47,subQ46,subQ45])],"isStart":false});var subQ66=sQuery(id+"F2.wireOp",EDGE,"E194.MirrorCS");var subQ67=sQuery(id+"F2.wireOp",EDGE,"E193.MirrorCS");var subQ68=sQuery(id+"F2.wireOp",EDGE,"E192.MirrorCS");Q1=makeQuery(id+"F3.boolean.opBoolean","SPLIT",FACE,{"disambiguationData":[TD([makeQuery(id+"F1.opExtrude","SWEPT_FACE",FACE,{"disambiguationData":[OSD([subQ40])]}),subQ65,makeQuery(id+"F1.opExtrude","SWEPT_FACE",FACE,{"disambiguationData":[OSD([subQ64])]}),makeQuery(id+"F1.opExtrude","SWEPT_FACE",FACE,{"disambiguationData":[OSD([subQ63])]}),makeQuery(id+"F1.opExtrude","SWEPT_FACE",FACE,{"disambiguationData":[OSD([subQ36,subQ35])]}),makeQuery(id+"F1.opExtrude","SWEPT_FACE",FACE,{"disambiguationData":[OSD([subQ34])]}),makeQuery(id+"F1.opExtrude","SWEPT_FACE",FACE,{"disambiguationData":[OSD([subQ37])]}),makeQuery(id+"F1.opExtrude","SWEPT_FACE",FACE,{"disambiguationData":[OSD([subQ43])]}),makeQuery(id+"F1.opExtrude","SWEPT_FACE",FACE,{"disambiguationData":[OSD([subQ32])]}),makeQuery(id+"F1.opExtrude","SWEPT_FACE",FACE,{"disambiguationData":[OSD([subQ30])]}),makeQuery(id+"F1.opExtrude","SWEPT_FACE",FACE,{"disambiguationData":[OSD([subQ62])]}),makeQuery(id+"F1.opExtrude","SWEPT_FACE",FACE,{"disambiguationData":[OSD([subQ61])]}),makeQuery(id+"F1.opExtrude","SWEPT_FACE",FACE,{"disambiguationData":[OSD([subQ60])]}),makeQuery(id+"F1.opExtrude","SWEPT_FACE",FACE,{"disambiguationData":[OSD([subQ59])]}),makeQuery(id+"F1.opExtrude","SWEPT_FACE",FACE,{"disambiguationData":[OSD([subQ41])]}),makeQuery(id+"F1.opExtrude","SWEPT_FACE",FACE,{"disambiguationData":[OSD([subQ58])]}),makeQuery(id+"F1.opExtrude","SWEPT_FACE",FACE,{"disambiguationData":[OSD([subQ57])]}),makeQuery(id+"F1.opExtrude","SWEPT_FACE",FACE,{"disambiguationData":[OSD([subQ56])]}),makeQuery(id+"F1.opExtrude","SWEPT_FACE",FACE,{"disambiguationData":[OSD([subQ55])]}),makeQuery(id+"F1.opExtrude","SWEPT_FACE",FACE,{"disambiguationData":[OSD([subQ54])]}),makeQuery(id+"F1.opExtrude","SWEPT_FACE",FACE,{"disambiguationData":[OSD([subQ53])]}),makeQuery(id+"F1.opExtrude","SWEPT_FACE",FACE,{"disambiguationData":[OSD([subQ52])]}),makeQuery(id+"F1.opExtrude","SWEPT_FACE",FACE,{"disambiguationData":[OSD([subQ29])]}),makeQuery(id+"F1.opExtrude","SWEPT_FACE",FACE,{"disambiguationData":[OSD([subQ28])]}),makeQuery(id+"F1.opExtrude","SWEPT_FACE",FACE,{"disambiguationData":[OSD([subQ27])]}),makeQuery(id+"F1.opExtrude","SWEPT_FACE",FACE,{"disambiguationData":[OSD([subQ26])]}),makeQuery(id+"F1.opExtrude","SWEPT_FACE",FACE,{"disambiguationData":[OSD([subQ25])]}),makeQuery(id+"F1.opExtrude","SWEPT_FACE",FACE,{"disambiguationData":[OSD([subQ24])]}),makeQuery(id+"F1.opExtrude","SWEPT_FACE",FACE,{"disambiguationData":[OSD([subQ23])]}),makeQuery(id+"F1.opExtrude","SWEPT_FACE",FACE,{"disambiguationData":[OSD([subQ22,subQ21])]}),makeQuery(id+"F1.opExtrude","SWEPT_FACE",FACE,{"disambiguationData":[OSD([subQ20])]}),makeQuery(id+"F1.opExtrude","SWEPT_FACE",FACE,{"disambiguationData":[OSD([subQ19])]}),makeQuery(id+"F1.opExtrude","SWEPT_FACE",FACE,{"disambiguationData":[OSD([subQ18])]}),makeQuery(id+"F1.opExtrude","SWEPT_FACE",FACE,{"disambiguationData":[OSD([subQ17])]}),makeQuery(id+"F1.opExtrude","SWEPT_FACE",FACE,{"disambiguationData":[OSD([subQ38])]}),makeQuery(id+"F1.opExtrude","SWEPT_FACE",FACE,{"disambiguationData":[OSD([subQ13])]}),makeQuery(id+"F1.opExtrude","SWEPT_FACE",FACE,{"disambiguationData":[OSD([subQ44])]}),makeQuery(id+"F1.opExtrude","SWEPT_FACE",FACE,{"disambiguationData":[OSD([subQ10])]}),makeQuery(id+"F1.opExtrude","SWEPT_FACE",FACE,{"disambiguationData":[OSD([subQ7])]}),makeQuery(id+"F1.opExtrude","SWEPT_FACE",FACE,{"disambiguationData":[OSD([subQ5])]}),makeQuery(id+"F1.opExtrude","SWEPT_FACE",FACE,{"disambiguationData":[OSD([subQ4])]}),makeQuery(id+"F1.opExtrude","SWEPT_FACE",FACE,{"disambiguationData":[OSD([subQ51])]}),makeQuery(id+"F1.opExtrude","SWEPT_FACE",FACE,{"disambiguationData":[OSD([subQ3])]}),makeQuery(id+"F1.opExtrude","SWEPT_FACE",FACE,{"disambiguationData":[OSD([subQ42])]}),makeQuery(id+"F1.opExtrude","SWEPT_FACE",FACE,{"disambiguationData":[OSD([subQ2,subQ1,subQ0])]}),makeQuery(id+"F1.opExtrude","SWEPT_FACE",FACE,{"disambiguationData":[OSD([subQ31])]}),makeQuery(id+"F1.opExtrude","SWEPT_FACE",FACE,{"disambiguationData":[OSD([subQ50])]}),makeQuery(id+"F1.opExtrude","SWEPT_FACE",FACE,{"disambiguationData":[OSD([subQ49])]}),makeQuery(id+"F1.opExtrude","SWEPT_FACE",FACE,{"disambiguationData":[OSD([subQ48])]}),makeQuery(id+"F1.opExtrude","SWEPT_FACE",FACE,{"disambiguationData":[OSD([subQ47])]}),makeQuery(id+"F1.opExtrude","SWEPT_FACE",FACE,{"disambiguationData":[OSD([subQ46])]}),makeQuery(id+"F1.opExtrude","SWEPT_FACE",FACE,{"disambiguationData":[OSD([subQ45])]}),makeQuery(id+"FvTl86mpc58GgTQ_2.opExtrude","SWEPT_FACE",FACE,{"disambiguationData":[OSD([subQ15])]}),subQ16,makeQuery(id+"FvTl86mpc58GgTQ_2.opExtrude","SWEPT_FACE",FACE,{"disambiguationData":[OSD([subQ14])]}),makeQuery(id+"FvTl86mpc58GgTQ_2.opExtrude","SWEPT_FACE",FACE,{"disambiguationData":[OSD([subQ11])]}),makeQuery(id+"FvTl86mpc58GgTQ_2.opExtrude","SWEPT_FACE",FACE,{"disambiguationData":[OSD([subQ8])]}),makeQuery(id+"F3.opExtrude","SWEPT_FACE",FACE,{"disambiguationData":[OSD([sQuery(id+"F2.wireOp",EDGE,"E181.MirrorCS")])]}),makeQuery(id+"F3.opExtrude","SWEPT_FACE",FACE,{"disambiguationData":[OSD([sQuery(id+"F2.wireOp",EDGE,"E182.MirrorCS")])]}),makeQuery(id+"F3.opExtrude","SWEPT_FACE",FACE,{"disambiguationData":[OSD([sQuery(id+"F2.wireOp",EDGE,"E186.MirrorCS")])]}),makeQuery(id+"F3.opExtrude","SWEPT_FACE",FACE,{"disambiguationData":[OSD([sQuery(id+"F2.wireOp",EDGE,"E180.MirrorCS")])]}),makeQuery(id+"F3.opExtrude","SWEPT_FACE",FACE,{"disambiguationData":[OSD([subQ33])]}),makeQuery(id+"F3.opExtrude","CAP_FACE",FACE,{"disambiguationData":[OSD([subQ33,sQuery(id+"F2.wireOp",EDGE,"E189.MirrorCS"),sQuery(id+"F2.wireOp",EDGE,"E190.MirrorCS"),sQuery(id+"F2.wireOp",EDGE,"E191.MirrorCS"),subQ12,subQ9,subQ6])],"isStart":true}),makeQuery(id+"F3.opExtrude","SWEPT_FACE",FACE,{"disambiguationData":[OSD([subQ68])]}),makeQuery(id+"F3.opExtrude","CAP_FACE",FACE,{"disambiguationData":[OSD([subQ68,subQ67,subQ66,subQ39,sQuery(id+"F2.wireOp",EDGE,"E214"),sQuery(id+"F2.wireOp",EDGE,"E215")])],"isStart":true}),makeQuery(id+"F3.opExtrude","SWEPT_FACE",FACE,{"disambiguationData":[OSD([subQ67])]}),makeQuery(id+"F3.opExtrude","SWEPT_FACE",FACE,{"disambiguationData":[OSD([subQ66])]}),makeQuery(id+"F3.opExtrude","SWEPT_FACE",FACE,{"disambiguationData":[OSD([sQuery(id+"F2.wireOp",EDGE,"E195.MirrorCS")])]}),makeQuery(id+"F3.opExtrude","SWEPT_FACE",FACE,{"disambiguationData":[OSD([sQuery(id+"F2.wireOp",EDGE,"E197.MirrorCS")])]}),makeQuery(id+"F3.opExtrude","SWEPT_FACE",FACE,{"disambiguationData":[OSD([sQuery(id+"F2.wireOp",EDGE,"E196.MirrorCS")])]}),makeQuery(id+"F3.opExtrude","SWEPT_FACE",FACE,{"disambiguationData":[OSD([sQuery(id+"F2.wireOp",EDGE,"E202.MirrorCS")])]}),makeQuery(id+"F3.opExtrude","SWEPT_FACE",FACE,{"disambiguationData":[OSD([sQuery(id+"F2.wireOp",EDGE,"E201.MirrorCS")])]}),makeQuery(id+"F3.opExtrude","SWEPT_FACE",FACE,{"disambiguationData":[OSD([sQuery(id+"F2.wireOp",EDGE,"E206")])]}),makeQuery(id+"F3.opExtrude","SWEPT_FACE",FACE,{"disambiguationData":[OSD([sQuery(id+"F2.wireOp",EDGE,"E207")])]}),makeQuery(id+"F3.opExtrude","SWEPT_FACE",FACE,{"disambiguationData":[OSD([subQ39])]}),makeQuery(id+"F3.opExtrude","SWEPT_FACE",FACE,{"disambiguationData":[OSD([subQ12])]}),makeQuery(id+"F3.opExtrude","SWEPT_FACE",FACE,{"disambiguationData":[OSD([subQ9])]}),makeQuery(id+"F3.opExtrude","SWEPT_FACE",FACE,{"disambiguationData":[OSD([subQ6])]})])],"derivedFrom":makeQuery(id+"FvTl86mpc58GgTQ_2.boolean.opBoolean","MERGE",FACE,{"derivedFrom":[subQ65,subQ16]})});}
            extrude(context, id + "F4", {"entities" : qUnion([Q0, Q1]), "depth" : 5.33 * mm, "offsetDistance" : 25.4 * mm});
        }
    });
